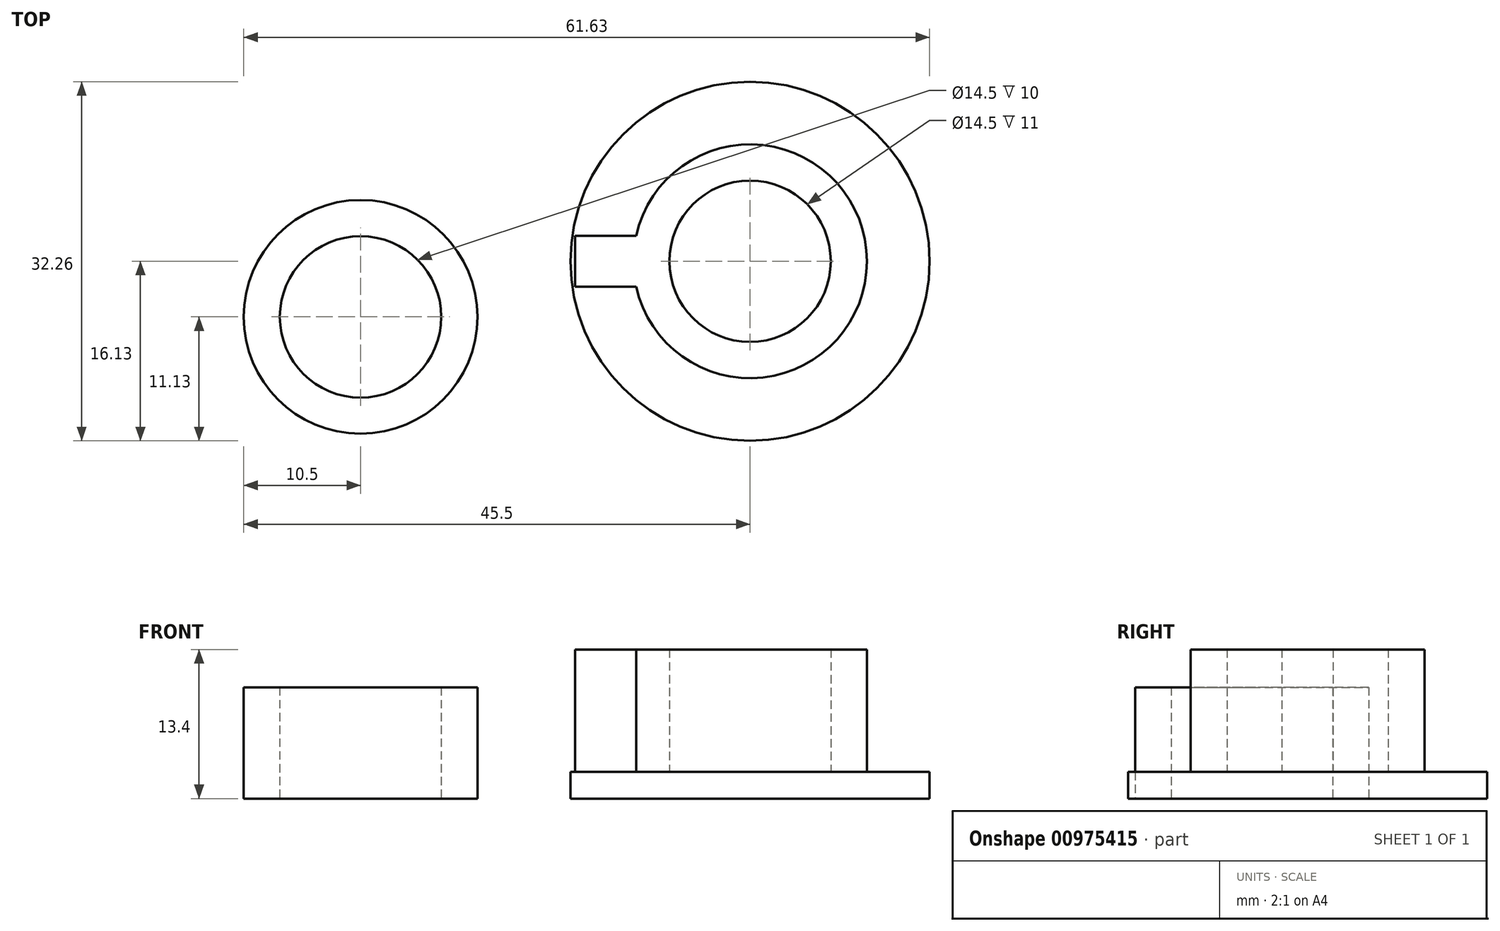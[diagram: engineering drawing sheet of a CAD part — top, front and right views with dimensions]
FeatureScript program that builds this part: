
annotation { "Feature Type Name" : "Feature", "Feature Type Description" : "" }
export const myFeature = defineFeature(function(context is Context, id is Id, definition is map)
    precondition{}
    {
        {
            var Q0;
            Q0=qCreatedBy(makeId("Top.planeOp"),FACE);
            var sketch = newSketch(context, id + "F0", { "sketchPlane" : qUnion([Q0])});
            skArc(sketch, "E0", {"start": v(3, -34.32) * mm, "mid": v(0, 34.45) * mm, "end": v(-3, -34.32) * mm});
            skArc(sketch, "E1", {"start": v(-10.4, -2.5) * mm, "mid": v(10.7, 0) * mm, "end": v(-10.4, 2.5) * mm});
            skLineSegment(sketch, "E2", {"start": v(3, -34.32) * mm, "end": v(3, -32.82) * mm});
            skLineSegment(sketch, "E3", {"start": v(3, -32.82) * mm, "end": v(0, -32.82) * mm});
            skLineSegment(sketch, "E4.MirrorCS", {"start": v(-3, -32.82) * mm, "end": v(0, -32.82) * mm});
            skLineSegment(sketch, "E5.MirrorCS", {"start": v(-3, -34.32) * mm, "end": v(-3, -32.82) * mm});
            skLineSegment(sketch, "E6", {"start": v(-10.4, 2.5) * mm, "end": v(-15.94, 2.5) * mm});
            skLineSegment(sketch, "E7", {"start": v(-15.94, 2.5) * mm, "end": v(-15.94, 0) * mm});
            skLineSegment(sketch, "E8.MirrorCS", {"start": v(-15.94, -2.5) * mm, "end": v(-15.94, 0) * mm});
            skLineSegment(sketch, "E9.MirrorCS", {"start": v(-10.4, -2.5) * mm, "end": v(-15.94, -2.5) * mm});
            skArc(sketch, "E10", {"start": v(-9.5, -11.21) * mm, "mid": v(-5.06, -13.8) * mm, "end": v(0, -14.7) * mm});
            skArc(sketch, "E11", {"start": v(-21.03, -22.03) * mm, "mid": v(-11.33, -28.27) * mm, "end": v(0, -30.45) * mm});
            skLineSegment(sketch, "E12.trimOffspring", {"start": v(-15.6, -10.93) * mm, "end": v(-20.44, -14.31) * mm});
            skArc(sketch, "E13.MirrorCS", {"start": v(9.5, -11.21) * mm, "mid": v(5.06, -13.8) * mm, "end": v(0, -14.7) * mm});
            skArc(sketch, "E14.MirrorCS", {"start": v(21.03, -22.03) * mm, "mid": v(11.33, -28.27) * mm, "end": v(0, -30.45) * mm});
            skLineSegment(sketch, "E15.MirrorCS", {"start": v(15.6, -10.93) * mm, "end": v(20.44, -14.31) * mm});
            skPoint(sketch, "E16.visualSharp", {"position": v(-12.04, -8.43) * mm});
            skArc(sketch, "E16.filletArc", {"start": v(-9.5, -11.21) * mm, "mid": v(-12.5, -10.03) * mm, "end": v(-15.6, -10.93) * mm});
            skPoint(sketch, "E17.visualSharp", {"position": v(12.04, -8.43) * mm});
            skArc(sketch, "E17.filletArc", {"start": v(15.6, -10.93) * mm, "mid": v(12.5, -10.03) * mm, "end": v(9.5, -11.21) * mm});
            skPoint(sketch, "E18.newPointA", {"position": v(24.08, -16.86) * mm});
            skPoint(sketch, "E18.newPointB", {"position": v(24.94, -17.47) * mm});
            skArc(sketch, "E18.filletArc", {"start": v(21.03, -22.03) * mm, "mid": v(22.56, -18.03) * mm, "end": v(20.44, -14.31) * mm});
            skPoint(sketch, "E19.newPointA", {"position": v(-24.08, -16.86) * mm});
            skPoint(sketch, "E19.newPointB", {"position": v(-24.94, -17.47) * mm});
            skArc(sketch, "E19.filletArc", {"start": v(-20.44, -14.31) * mm, "mid": v(-22.56, -18.03) * mm, "end": v(-21.03, -22.03) * mm});
            skSolve(sketch);
        }
        {
            var Q0;
            Q0=qCreatedBy(makeId("Top.planeOp"),FACE);
            var sketch = newSketch(context, id + "F1", { "sketchPlane" : qUnion([Q0])});
            skCircle(sketch, "E20", {"center": v(0, 0) * mm, "radius": 7.25 * mm});
            skLineSegment(sketch, "E21.0", {"start": v(-10.4, 2.5) * mm, "end": v(-15.94, 2.5) * mm});
            skLineSegment(sketch, "E22.0.0", {"start": v(-15.94, -2.5) * mm, "end": v(-10.4, -2.5) * mm});
            skArc(sketch, "E22.0.1", {"start": v(-10.4, -2.5) * mm, "mid": v(10.7, 0) * mm, "end": v(-10.4, 2.5) * mm});
            skLineSegment(sketch, "E22.0.3", {"start": v(-15.94, 2.5) * mm, "end": v(-15.94, 0) * mm});
            skLineSegment(sketch, "E22.0.4", {"start": v(-15.94, 0) * mm, "end": v(-15.94, -2.5) * mm});
            skLineSegment(sketch, "E23.0", {"start": v(-10.24, 2.3) * mm, "end": v(-15.74, 2.3) * mm});
            skArc(sketch, "E23.1", {"start": v(-10.24, -2.3) * mm, "mid": v(10.5, 0) * mm, "end": v(-10.24, 2.3) * mm});
            skLineSegment(sketch, "E23.2", {"start": v(-15.74, 2.3) * mm, "end": v(-15.74, 0) * mm});
            skLineSegment(sketch, "E23.3", {"start": v(-15.74, 0) * mm, "end": v(-15.74, -2.3) * mm});
            skLineSegment(sketch, "E23.4", {"start": v(-15.74, -2.3) * mm, "end": v(-10.24, -2.3) * mm});
            skCircle(sketch, "E24", {"center": v(0, 0) * mm, "radius": 16.13 * mm});
            skSolve(sketch);
        }
        {
            var Q0;
            Q0=qCreatedBy(makeId("Top.planeOp"),FACE);
            var sketch = newSketch(context, id + "F2", { "sketchPlane" : qUnion([Q0])});
            skCircle(sketch, "E25.0", {"center": v(0, 0) * mm, "radius": 7.25 * mm});
            skPoint(sketch, "E26.0", {"position": v(-10.24, 2.3) * mm});
            skCircle(sketch, "E27", {"center": v(0, 0) * mm, "radius": 10.5 * mm});
            skSolve(sketch);
        }
        {
            var Q0;
            Q0=makeQuery(id+"F1.imprint","IMPRINT",FACE,{"disambiguationData":[TD([[makeQuery(id+"F1.imprint","IMPRINT",EDGE,{"derivedFrom":sQuery(id+"F1.wireOp",EDGE,"E20")}),-1.0]])]});
            extrude(context, id + "F3", {"entities" : qUnion([Q0]), "oppositeDirection" : true, "depth" : 11 * mm, "offsetDistance" : 25 * mm});
        }
        {
            var Q0;
            Q0 = qSketchRegion(id + "F1", true);
            var Q1;
            Q1=makeQuery(id+"F1.imprint","IMPRINT",FACE,{"disambiguationData":[TD([[makeQuery(id+"F1.imprint","IMPRINT",EDGE,{"derivedFrom":sQuery(id+"F1.wireOp",EDGE,"E20")}),-1.0]])]});
            var Q2;
            Q2=makeQuery(id+"F1.imprint","IMPRINT",FACE,{"disambiguationData":[TD([[makeQuery(id+"F1.imprint","IMPRINT",EDGE,{"derivedFrom":sQuery(id+"F1.wireOp",EDGE,"E20")}),1.0]])]});
            extrude(context, id + "F4", {"entities" : qUnion([Q0, Q1, Q2]), "operationType" : NewBodyOperationType.ADD, "depth" : 2.4 * mm, "offsetDistance" : 25 * mm});
        }
        {
            var Q0;
            Q0=makeQuery(id+"F3.opExtrude","SWEPT_BODY",BODY,{"disambiguationData":[OSD([sQuery(id+"F1.wireOp",EDGE,"E20"),sQuery(id+"F1.wireOp",EDGE,"E23.0"),sQuery(id+"F1.wireOp",EDGE,"E23.1"),sQuery(id+"F1.wireOp",EDGE,"E23.2"),sQuery(id+"F1.wireOp",EDGE,"E23.3"),sQuery(id+"F1.wireOp",EDGE,"E23.4")])]});
            transform(context, id + "F5", {"entities" : qUnion([Q0]), "transformType" : TransformType.TRANSLATION_3D, "dx" : 35 * mm, "dy" : 0 * mm, "dz" : -2.4 * mm, "makeCopy" : false});
        }
        {
            var Q0;
            Q0=makeQuery(id+"F3.opExtrude","SWEPT_BODY",BODY,{"disambiguationData":[OSD([sQuery(id+"F1.wireOp",EDGE,"E20"),sQuery(id+"F1.wireOp",EDGE,"E23.0"),sQuery(id+"F1.wireOp",EDGE,"E23.1"),sQuery(id+"F1.wireOp",EDGE,"E23.2"),sQuery(id+"F1.wireOp",EDGE,"E23.3"),sQuery(id+"F1.wireOp",EDGE,"E23.4")])]});
            var Q1;
            Q1=sQuery(id+"F0.wireOp",EDGE,"E6");
            transform(context, id + "F6", {"entities" : qUnion([Q0]), "transformType" : TransformType.ROTATION, "transformAxis" : qUnion([Q1]), "angle" : 180 * degree, "makeCopy" : false});
        }
        {
            var Q0;
            Q0=makeQuery(id+"F2.imprint","IMPRINT",FACE,{"disambiguationData":[TD([[makeQuery(id+"F2.imprint","IMPRINT",EDGE,{"derivedFrom":sQuery(id+"F2.wireOp",EDGE,"E25.0")}),-1.0]])]});
            extrude(context, id + "F7", {"entities" : qUnion([Q0]), "depth" : 10 * mm, "offsetDistance" : 25 * mm});
        }
    });
